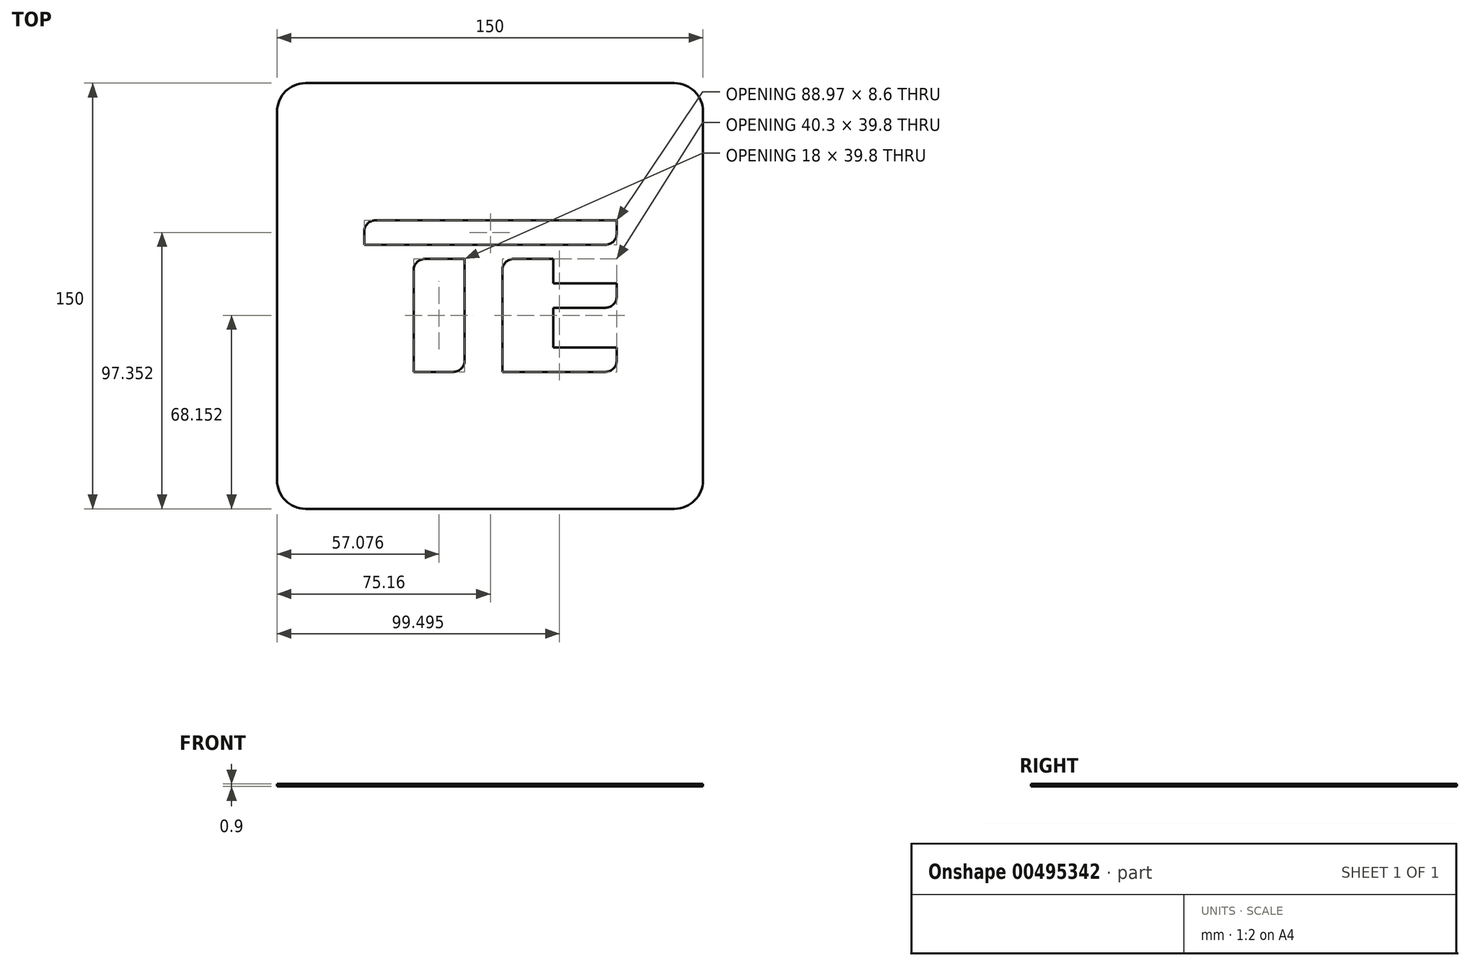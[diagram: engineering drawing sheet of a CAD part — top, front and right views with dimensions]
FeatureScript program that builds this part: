
annotation { "Feature Type Name" : "Feature", "Feature Type Description" : "" }
export const myFeature = defineFeature(function(context is Context, id is Id, definition is map)
    precondition{}
    {
        {
            var Q0;
            Q0=qCreatedBy(makeId("Top.planeOp"),FACE);
            var sketch = newSketch(context, id + "F0", { "sketchPlane" : qUnion([Q0])});
            skLineSegment(sketch, "E0.bottom", {"start": v(63.3, 34.79) * mm, "end": v(20.8, 34.79) * mm});
            skLineSegment(sketch, "E0.top", {"start": v(65.3, 39.09) * mm, "end": v(22.8, 39.09) * mm});
            skLineSegment(sketch, "E0.left", {"start": v(65.3, 36.79) * mm, "end": v(65.3, 39.09) * mm});
            skLineSegment(sketch, "E0.right", {"start": v(20.8, 34.79) * mm, "end": v(20.8, 37.09) * mm});
            skPoint(sketch, "E0.middle", {"position": v(43.05, 36.94) * mm});
            skPoint(sketch, "E1.visualSharp", {"position": v(20.8, 39.09) * mm});
            skArc(sketch, "E1.filletArc", {"start": v(22.8, 39.09) * mm, "mid": v(21.4, 38.5) * mm, "end": v(20.8, 37.09) * mm});
            skPoint(sketch, "E2.visualSharp", {"position": v(65.3, 34.79) * mm});
            skArc(sketch, "E2.filletArc", {"start": v(63.3, 34.79) * mm, "mid": v(64.7, 35.37) * mm, "end": v(65.3, 36.79) * mm});
            skLineSegment(sketch, "E3.bottom", {"start": v(38.5, 32.29) * mm, "end": v(31.5, 32.29) * mm});
            skLineSegment(sketch, "E3.top", {"start": v(36.5, 12.39) * mm, "end": v(29.5, 12.39) * mm});
            skLineSegment(sketch, "E3.left", {"start": v(38.5, 32.29) * mm, "end": v(38.5, 14.39) * mm});
            skLineSegment(sketch, "E3.right", {"start": v(29.5, 30.29) * mm, "end": v(29.5, 12.39) * mm});
            skPoint(sketch, "E3.middle", {"position": v(34, 22.34) * mm});
            skPoint(sketch, "E4.visualSharp", {"position": v(29.5, 32.29) * mm});
            skArc(sketch, "E4.filletArc", {"start": v(31.5, 32.29) * mm, "mid": v(30.1, 31.7) * mm, "end": v(29.5, 30.29) * mm});
            skPoint(sketch, "E5.visualSharp", {"position": v(38.5, 12.39) * mm});
            skArc(sketch, "E5.filletArc", {"start": v(36.5, 12.39) * mm, "mid": v(37.92, 12.97) * mm, "end": v(38.5, 14.39) * mm});
            skLineSegment(sketch, "E6.bottom", {"start": v(54.14, 32.29) * mm, "end": v(47.14, 32.29) * mm});
            skLineSegment(sketch, "E6.top", {"start": v(54.14, 12.39) * mm, "end": v(45.14, 12.39) * mm});
            skLineSegment(sketch, "E6.left", {"start": v(54.14, 32.29) * mm, "end": v(54.14, 12.39) * mm});
            skLineSegment(sketch, "E6.right", {"start": v(45.14, 30.29) * mm, "end": v(45.14, 12.39) * mm});
            skPoint(sketch, "E6.middle", {"position": v(49.64, 22.34) * mm});
            skLineSegment(sketch, "E7.bottom", {"start": v(54.14, 12.39) * mm, "end": v(63.3, 12.39) * mm});
            skLineSegment(sketch, "E7.top", {"start": v(54.14, 16.69) * mm, "end": v(65.3, 16.69) * mm});
            skLineSegment(sketch, "E7.left", {"start": v(54.14, 12.39) * mm, "end": v(54.14, 16.69) * mm});
            skLineSegment(sketch, "E7.right", {"start": v(65.3, 14.39) * mm, "end": v(65.3, 16.69) * mm});
            skPoint(sketch, "E7.middle", {"position": v(59.72, 14.54) * mm});
            skLineSegment(sketch, "E8.bottom", {"start": v(54.14, 23.69) * mm, "end": v(63.3, 23.69) * mm});
            skLineSegment(sketch, "E8.top", {"start": v(54.14, 27.99) * mm, "end": v(65.3, 27.99) * mm});
            skLineSegment(sketch, "E8.left", {"start": v(54.14, 23.69) * mm, "end": v(54.14, 27.99) * mm});
            skLineSegment(sketch, "E8.right", {"start": v(65.3, 25.69) * mm, "end": v(65.3, 27.99) * mm});
            skPoint(sketch, "E8.middle", {"position": v(59.72, 25.84) * mm});
            skPoint(sketch, "E9.visualSharp", {"position": v(65.3, 23.69) * mm});
            skArc(sketch, "E9.filletArc", {"start": v(63.3, 23.69) * mm, "mid": v(64.7, 24.27) * mm, "end": v(65.3, 25.69) * mm});
            skPoint(sketch, "E10.visualSharp", {"position": v(65.3, 12.39) * mm});
            skArc(sketch, "E10.filletArc", {"start": v(63.3, 12.39) * mm, "mid": v(64.7, 12.97) * mm, "end": v(65.3, 14.39) * mm});
            skPoint(sketch, "E11.visualSharp", {"position": v(45.14, 32.29) * mm});
            skArc(sketch, "E11.filletArc", {"start": v(47.14, 32.29) * mm, "mid": v(45.73, 31.7) * mm, "end": v(45.14, 30.29) * mm});
            skSolve(sketch);
        }
        {
            var Q0;
            Q0=qCreatedBy(makeId("Top.planeOp"),FACE);
            var sketch = newSketch(context, id + "F1", { "sketchPlane" : qUnion([Q0])});
            skPoint(sketch, "E12.0", {"position": v(0, 51.52) * mm});
            skPoint(sketch, "E13.0", {"position": v(85.94, 51.52) * mm});
            skPoint(sketch, "E14.0", {"position": v(85.94, 0) * mm});
            skLineSegment(sketch, "E15", {"start": v(0, 51.52) * mm, "end": v(85.94, 0) * mm, "construction": true});
            skLineSegment(sketch, "E16", {"start": v(85.94, 51.52) * mm, "end": v(0, 0) * mm, "construction": true});
            skLineSegment(sketch, "E17.bottom", {"start": v(80.47, 63.26) * mm, "end": v(5.47, 63.26) * mm});
            skLineSegment(sketch, "E17.top", {"start": v(80.47, -11.74) * mm, "end": v(5.47, -11.74) * mm});
            skLineSegment(sketch, "E17.left", {"start": v(80.47, 63.26) * mm, "end": v(80.47, -11.74) * mm});
            skLineSegment(sketch, "E17.right", {"start": v(5.47, 63.26) * mm, "end": v(5.47, -11.74) * mm});
            skPoint(sketch, "E17.middle", {"position": v(42.97, 25.76) * mm});
            skSolve(sketch);
        }
        {
            var Q0;
            Q0 = qSketchRegion(id + "F1", true);
            extrude(context, id + "F2", {"entities" : qUnion([Q0]), "depth" : (.9 / 2) * mm});
        }
        {
            var Q0;
            Q0 = qSketchRegion(id + "F0", true);
            extrude(context, id + "F3", {"entities" : qUnion([Q0]), "operationType" : NewBodyOperationType.REMOVE, "endBound" : BoundingType.THROUGH_ALL, "depth" : 25 * mm});
        }
        {
            var Q0;
            Q0=makeQuery(id+"F2.opExtrude","SWEPT_BODY",BODY,{"disambiguationData":[OSD([sQuery(id+"F1.wireOp",EDGE,"E17.bottom"),sQuery(id+"F1.wireOp",EDGE,"E17.top"),sQuery(id+"F1.wireOp",EDGE,"E17.left"),sQuery(id+"F1.wireOp",EDGE,"E17.right")])]});
            var Q1;
            Q1=qCreatedBy(makeId("Origin.pointOp"),VERTEX);
            transform(context, id + "F4", {"entities" : qUnion([Q0]), "transformType" : TransformType.SCALE_UNIFORMLY, "scale" : 2, "scalePoint" : qUnion([Q1]), "makeCopy" : false});
        }
        {
            var Q0;
            Q0=makeQuery(id+"F2.opExtrude","SWEPT_EDGE",EDGE,{"disambiguationData":[OSD([sQuery(id+"F1.wireOp",EDGE,"E17.top"),sQuery(id+"F1.wireOp",EDGE,"E17.left")])]});
            var Q1;
            Q1=makeQuery(id+"F2.opExtrude","SWEPT_EDGE",EDGE,{"disambiguationData":[OSD([sQuery(id+"F1.wireOp",EDGE,"E17.top"),sQuery(id+"F1.wireOp",EDGE,"E17.right")])]});
            var Q2;
            Q2=makeQuery(id+"F2.opExtrude","SWEPT_EDGE",EDGE,{"disambiguationData":[OSD([sQuery(id+"F1.wireOp",EDGE,"E17.bottom"),sQuery(id+"F1.wireOp",EDGE,"E17.right")])]});
            var Q3;
            Q3=makeQuery(id+"F2.opExtrude","SWEPT_EDGE",EDGE,{"disambiguationData":[OSD([sQuery(id+"F1.wireOp",EDGE,"E17.bottom"),sQuery(id+"F1.wireOp",EDGE,"E17.left")])]});
            fillet(context, id + "F5", {"entities" : qUnion([Q0, Q1, Q2, Q3]), "radius" : 10 * mm, "tangentPropagation" : true, "allowEdgeOverflow" : false});
        }
    });
